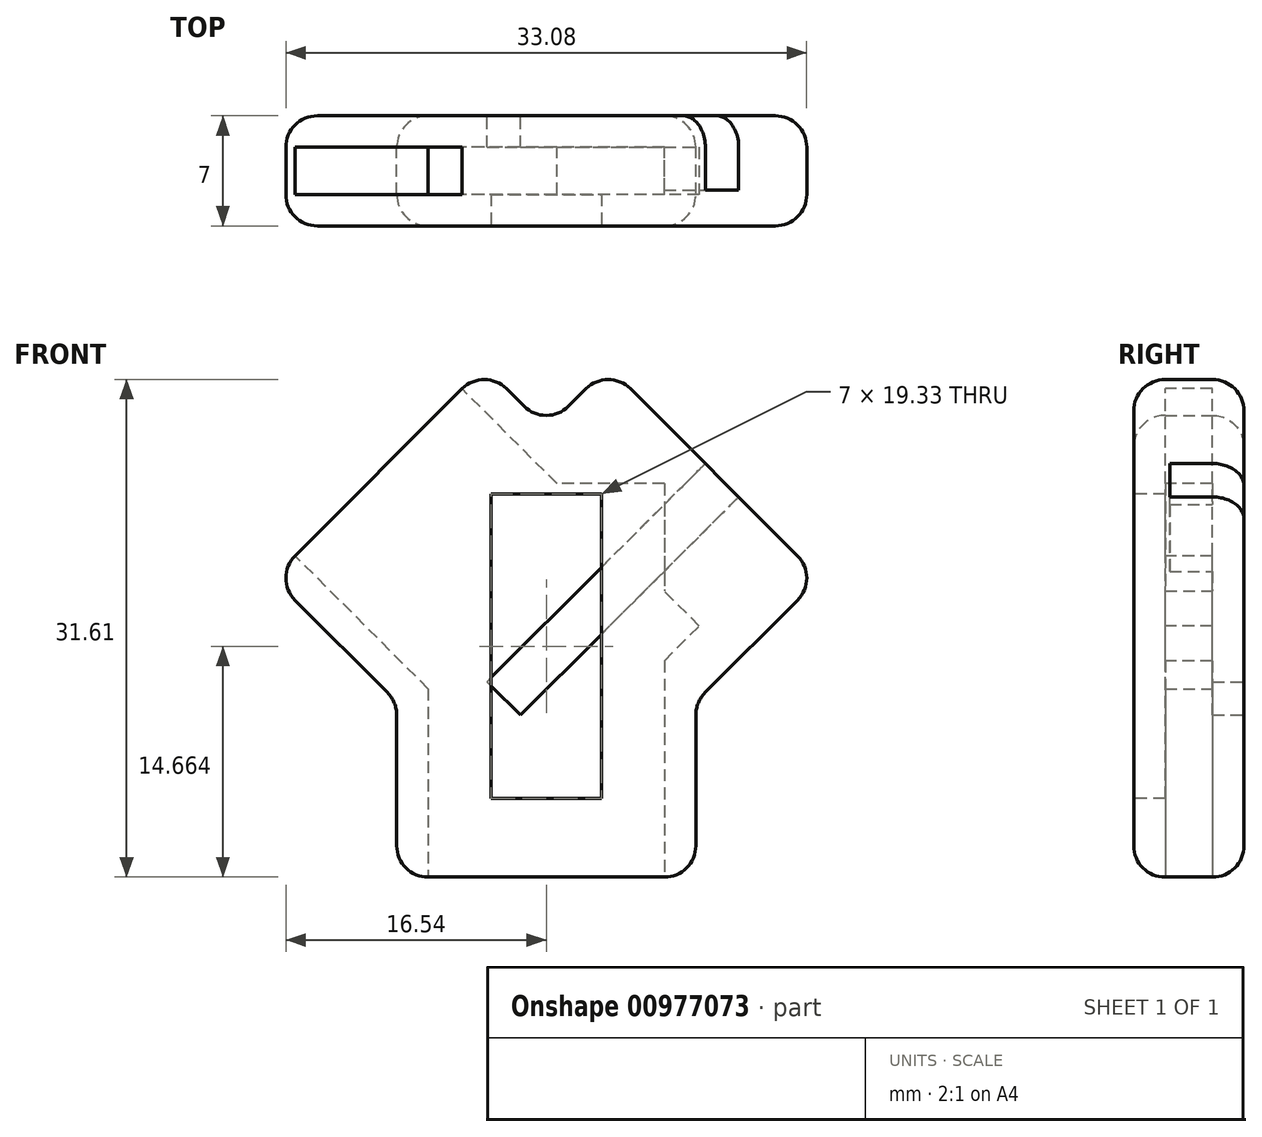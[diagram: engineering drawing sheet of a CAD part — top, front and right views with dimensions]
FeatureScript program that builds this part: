
annotation { "Feature Type Name" : "Feature", "Feature Type Description" : "" }
export const myFeature = defineFeature(function(context is Context, id is Id, definition is map)
    precondition{}
    {
        {
            var Q0;
            Q0=qCreatedBy(makeId("Front.planeOp"),FACE);
            var sketch = newSketch(context, id + "F0", { "sketchPlane" : qUnion([Q0])});
            skLineSegment(sketch, "E0.bottom", {"start": v(-9.5, 0) * mm, "end": v(9.5, 0) * mm});
            skLineSegment(sketch, "E0.top", {"start": v(-9.5, -19) * mm, "end": v(9.5, -19) * mm});
            skLineSegment(sketch, "E0.left", {"start": v(-9.5, 0) * mm, "end": v(-9.5, -19) * mm});
            skLineSegment(sketch, "E0.right", {"start": v(9.5, 0) * mm, "end": v(9.5, -19) * mm});
            skLineSegment(sketch, "E1", {"start": v(-9.5, 0) * mm, "end": v(3.94, 13.44) * mm});
            skLineSegment(sketch, "E2", {"start": v(3.94, 13.44) * mm, "end": v(17.37, 0) * mm});
            skLineSegment(sketch, "E3", {"start": v(17.37, 0) * mm, "end": v(9.5, -7.87) * mm});
            skLineSegment(sketch, "E4", {"start": v(9.5, -7.87) * mm, "end": v(9.5, 0) * mm});
            skLineSegment(sketch, "E5", {"start": v(9.5, 0) * mm, "end": v(-3.94, 13.44) * mm});
            skLineSegment(sketch, "E6", {"start": v(-3.94, 13.44) * mm, "end": v(-17.37, 0) * mm});
            skLineSegment(sketch, "E7", {"start": v(-17.37, 0) * mm, "end": v(-9.5, -7.87) * mm});
            skSolve(sketch);
        }
        {
            var Q0;
            Q0 = qSketchRegion(id + "F0", true);
            extrude(context, id + "F1", {"entities" : qUnion([Q0]), "depth" : 7 * mm, "offsetDistance" : 25 * mm});
        }
        {
            var Q0;
            Q0=makeQuery(id+"F1.opExtrude","SWEPT_FACE",FACE,{"disambiguationData":[OSD([sQuery(id+"F0.wireOp",EDGE,"E0.top")])]});
            var sketch = newSketch(context, id + "F2", { "sketchPlane" : qUnion([Q0])});
            skLineSegment(sketch, "E8.bottom", {"start": v(7.5, 2) * mm, "end": v(-7.5, 2) * mm});
            skLineSegment(sketch, "E8.top", {"start": v(7.5, 5) * mm, "end": v(-7.5, 5) * mm});
            skLineSegment(sketch, "E8.left", {"start": v(7.5, 2) * mm, "end": v(7.5, 5) * mm});
            skLineSegment(sketch, "E8.right", {"start": v(-7.5, 2) * mm, "end": v(-7.5, 5) * mm});
            skPoint(sketch, "E8.middle", {"position": v(0, 3.5) * mm});
            skPoint(sketch, "E8.middle.positionSnap0", {"position": v(0, 7) * mm});
            skPoint(sketch, "E8.middle.positionSnap1", {"position": v(-9.5, 3.5) * mm});
            skPoint(sketch, "E8.centerSnap0", {"position": v(0, 7) * mm});
            skPoint(sketch, "E8.centerSnap1", {"position": v(-9.5, 3.5) * mm});
            skSolve(sketch);
        }
        {
            var Q0;
            Q0 = qSketchRegion(id + "F2", true);
            extrude(context, id + "F3", {"entities" : qUnion([Q0]), "operationType" : NewBodyOperationType.REMOVE, "oppositeDirection" : true, "depth" : 25 * mm, "offsetDistance" : 25 * mm});
        }
        {
            var Q0;
            Q0=makeQuery(id+"F1.opExtrude","SWEPT_FACE",FACE,{"disambiguationData":[OSD([sQuery(id+"F0.wireOp",EDGE,"E2")])]});
            var sketch = newSketch(context, id + "F4", { "sketchPlane" : qUnion([Q0])});
            skLineSegment(sketch, "E9.bottom", {"start": v(-4.72, -2) * mm, "end": v(10.28, -2) * mm});
            skLineSegment(sketch, "E9.top", {"start": v(-4.72, -5) * mm, "end": v(10.28, -5) * mm});
            skLineSegment(sketch, "E9.left", {"start": v(-4.72, -2) * mm, "end": v(-4.72, -5) * mm});
            skLineSegment(sketch, "E9.right", {"start": v(10.28, -2) * mm, "end": v(10.28, -5) * mm});
            skPoint(sketch, "E9.middle", {"position": v(2.78, -3.5) * mm});
            skPoint(sketch, "E9.middle.positionSnap0", {"position": v(12.28, -3.5) * mm});
            skPoint(sketch, "E9.middle.positionSnap1", {"position": v(2.78, 0) * mm});
            skPoint(sketch, "E9.centerSnap0", {"position": v(12.28, -3.5) * mm});
            skPoint(sketch, "E9.centerSnap1", {"position": v(2.78, 0) * mm});
            skSolve(sketch);
        }
        {
            var Q0;
            Q0 = qSketchRegion(id + "F4", true);
            extrude(context, id + "F5", {"entities" : qUnion([Q0]), "operationType" : NewBodyOperationType.REMOVE, "oppositeDirection" : true, "depth" : 19.6 * mm, "offsetDistance" : 25 * mm});
        }
        {
            var Q0;
            Q0=makeQuery(id+"F1.opExtrude","SWEPT_FACE",FACE,{"disambiguationData":[OSD([sQuery(id+"F0.wireOp",EDGE,"E6")])]});
            var sketch = newSketch(context, id + "F6", { "sketchPlane" : qUnion([Q0])});
            skLineSegment(sketch, "E10.bottom", {"start": v(2, -10.28) * mm, "end": v(5, -10.28) * mm});
            skLineSegment(sketch, "E10.top", {"start": v(2, 4.72) * mm, "end": v(5, 4.72) * mm});
            skLineSegment(sketch, "E10.left", {"start": v(2, -10.28) * mm, "end": v(2, 4.72) * mm});
            skLineSegment(sketch, "E10.right", {"start": v(5, -10.28) * mm, "end": v(5, 4.72) * mm});
            skPoint(sketch, "E10.middle", {"position": v(3.5, -2.78) * mm});
            skPoint(sketch, "E10.middle.positionSnap0", {"position": v(0, -2.78) * mm});
            skPoint(sketch, "E10.middle.positionSnap1", {"position": v(3.5, 6.72) * mm});
            skPoint(sketch, "E10.centerSnap0", {"position": v(0, -2.78) * mm});
            skPoint(sketch, "E10.centerSnap1", {"position": v(3.5, 6.72) * mm});
            skSolve(sketch);
        }
        {
            var Q0;
            Q0 = qSketchRegion(id + "F6", true);
            extrude(context, id + "F7", {"entities" : qUnion([Q0]), "operationType" : NewBodyOperationType.REMOVE, "oppositeDirection" : true, "depth" : 21.3 * mm, "offsetDistance" : 25 * mm});
        }
        {
            var Q0;
            Q0=makeQuery(id+"F1.opExtrude","CAP_EDGE",EDGE,{"disambiguationData":[OSD([sQuery(id+"F0.wireOp",EDGE,"E0.left")])],"isStart":false});
            var Q1;
            Q1=makeQuery(id+"F1.opExtrude","CAP_EDGE",EDGE,{"disambiguationData":[OSD([sQuery(id+"F0.wireOp",EDGE,"E7")])],"isStart":false});
            var Q2;
            Q2=makeQuery(id+"F1.opExtrude","CAP_EDGE",EDGE,{"disambiguationData":[OSD([sQuery(id+"F0.wireOp",EDGE,"E7")])],"isStart":true});
            var Q3;
            Q3=makeQuery(id+"F1.opExtrude","CAP_EDGE",EDGE,{"disambiguationData":[OSD([sQuery(id+"F0.wireOp",EDGE,"E0.left")])],"isStart":true});
            var Q4;
            Q4=makeQuery(id+"F1.opExtrude","CAP_EDGE",EDGE,{"disambiguationData":[OSD([sQuery(id+"F0.wireOp",EDGE,"E0.top")])],"isStart":false});
            var Q5;
            Q5=makeQuery(id+"F1.opExtrude","CAP_EDGE",EDGE,{"disambiguationData":[OSD([sQuery(id+"F0.wireOp",EDGE,"E0.top")])],"isStart":true});
            var Q6;
            Q6=makeQuery(id+"F1.opExtrude","SWEPT_EDGE",EDGE,{"disambiguationData":[OSD([sQuery(id+"F0.wireOp",EDGE,"E0.top"),sQuery(id+"F0.wireOp",EDGE,"E0.left")])]});
            var Q7;
            Q7=makeQuery(id+"F1.opExtrude","SWEPT_EDGE",EDGE,{"disambiguationData":[OSD([sQuery(id+"F0.wireOp",EDGE,"E0.top"),sQuery(id+"F0.wireOp",EDGE,"E0.right")])]});
            var Q8;
            Q8=makeQuery(id+"F1.opExtrude","CAP_EDGE",EDGE,{"disambiguationData":[OSD([sQuery(id+"F0.wireOp",EDGE,"E0.right")])],"isStart":false});
            var Q9;
            Q9=makeQuery(id+"F1.opExtrude","CAP_EDGE",EDGE,{"disambiguationData":[OSD([sQuery(id+"F0.wireOp",EDGE,"E0.right")])],"isStart":true});
            var Q10;
            Q10=makeQuery(id+"F1.opExtrude","CAP_EDGE",EDGE,{"disambiguationData":[OSD([sQuery(id+"F0.wireOp",EDGE,"E3")])],"isStart":true});
            var Q11;
            Q11=makeQuery(id+"F1.opExtrude","CAP_EDGE",EDGE,{"disambiguationData":[OSD([sQuery(id+"F0.wireOp",EDGE,"E3")])],"isStart":false});
            var Q12;
            Q12=makeQuery(id+"F1.opExtrude","SWEPT_EDGE",EDGE,{"disambiguationData":[OSD([sQuery(id+"F0.wireOp",EDGE,"E2"),sQuery(id+"F0.wireOp",EDGE,"E3")])]});
            var Q13;
            Q13=makeQuery(id+"F1.opExtrude","CAP_EDGE",EDGE,{"disambiguationData":[OSD([sQuery(id+"F0.wireOp",EDGE,"E2")])],"isStart":false});
            var Q14;
            Q14=makeQuery(id+"F1.opExtrude","SWEPT_EDGE",EDGE,{"disambiguationData":[OSD([sQuery(id+"F0.wireOp",EDGE,"E1"),sQuery(id+"F0.wireOp",EDGE,"E2")])]});
            var Q15;
            Q15=makeQuery(id+"F1.opExtrude","CAP_EDGE",EDGE,{"disambiguationData":[OSD([sQuery(id+"F0.wireOp",EDGE,"E2")])],"isStart":true});
            var Q16;
            Q16=makeQuery(id+"F1.opExtrude","CAP_EDGE",EDGE,{"disambiguationData":[OSD([sQuery(id+"F0.wireOp",EDGE,"E1")])],"isStart":true});
            var Q17;
            Q17=makeQuery(id+"F1.opExtrude","CAP_EDGE",EDGE,{"disambiguationData":[OSD([sQuery(id+"F0.wireOp",EDGE,"E5")])],"isStart":true});
            var Q18;
            Q18=makeQuery(id+"F1.opExtrude","CAP_EDGE",EDGE,{"disambiguationData":[OSD([sQuery(id+"F0.wireOp",EDGE,"E5")])],"isStart":false});
            var Q19;
            Q19=makeQuery(id+"F1.opExtrude","CAP_EDGE",EDGE,{"disambiguationData":[OSD([sQuery(id+"F0.wireOp",EDGE,"E1")])],"isStart":false});
            var Q20;
            Q20=makeQuery(id+"F1.opExtrude","CAP_EDGE",EDGE,{"disambiguationData":[OSD([sQuery(id+"F0.wireOp",EDGE,"E6")])],"isStart":false});
            var Q21;
            Q21=makeQuery(id+"F1.opExtrude","SWEPT_EDGE",EDGE,{"disambiguationData":[OSD([sQuery(id+"F0.wireOp",EDGE,"E5"),sQuery(id+"F0.wireOp",EDGE,"E6")])]});
            var Q22;
            Q22=makeQuery(id+"F1.opExtrude","CAP_EDGE",EDGE,{"disambiguationData":[OSD([sQuery(id+"F0.wireOp",EDGE,"E6")])],"isStart":true});
            var Q23;
            Q23=makeQuery(id+"F1.opExtrude","SWEPT_EDGE",EDGE,{"disambiguationData":[OSD([sQuery(id+"F0.wireOp",EDGE,"E6"),sQuery(id+"F0.wireOp",EDGE,"E7")])]});
            var Q24;
            Q24=makeQuery(id+"F1.opExtrude","SWEPT_EDGE",EDGE,{"disambiguationData":[OSD([sQuery(id+"F0.wireOp",EDGE,"E1"),sQuery(id+"F0.wireOp",EDGE,"E5")])]});
            var Q25;
            Q25=makeQuery(id+"F1.opExtrude","SWEPT_EDGE",EDGE,{"disambiguationData":[OSD([sQuery(id+"F0.wireOp",EDGE,"E0.left"),sQuery(id+"F0.wireOp",EDGE,"E7")])]});
            var Q26;
            Q26=makeQuery(id+"F1.opExtrude","SWEPT_EDGE",EDGE,{"disambiguationData":[OSD([sQuery(id+"F0.wireOp",EDGE,"E0.right"),sQuery(id+"F0.wireOp",EDGE,"E3"),sQuery(id+"F0.wireOp",EDGE,"E4")])]});
            fillet(context, id + "F8", {"entities" : qUnion([Q0, Q1, Q2, Q3, Q4, Q5, Q6, Q7, Q8, Q9, Q10, Q11, Q12, Q13, Q14, Q15, Q16, Q17, Q18, Q19, Q20, Q21, Q22, Q23, Q24, Q25, Q26]), "radius" : 2 * mm, "tangentPropagation" : true, "allowEdgeOverflow" : false});
        }
        {
            var Q0;
            Q0=makeQuery(id+"F1.opExtrude","CAP_FACE",FACE,{"disambiguationData":[OSD([sQuery(id+"F0.wireOp",EDGE,"E0.top"),sQuery(id+"F0.wireOp",EDGE,"E0.left"),sQuery(id+"F0.wireOp",EDGE,"E0.right"),sQuery(id+"F0.wireOp",EDGE,"E1"),sQuery(id+"F0.wireOp",EDGE,"E2"),sQuery(id+"F0.wireOp",EDGE,"E3"),sQuery(id+"F0.wireOp",EDGE,"E5"),sQuery(id+"F0.wireOp",EDGE,"E6"),sQuery(id+"F0.wireOp",EDGE,"E7")])],"isStart":false});
            var sketch = newSketch(context, id + "F9", { "sketchPlane" : qUnion([Q0])});
            skLineSegment(sketch, "E11.bottom", {"start": v(-3.5, -14) * mm, "end": v(3.5, -14) * mm});
            skLineSegment(sketch, "E11.top", {"start": v(-3.5, 5.33) * mm, "end": v(3.5, 5.33) * mm});
            skLineSegment(sketch, "E11.left", {"start": v(-3.5, -14) * mm, "end": v(-3.5, 5.33) * mm});
            skLineSegment(sketch, "E11.right", {"start": v(3.5, -14) * mm, "end": v(3.5, 5.33) * mm});
            skSolve(sketch);
        }
        {
            var Q0;
            Q0 = qSketchRegion(id + "F9", true);
            extrude(context, id + "F10", {"entities" : qUnion([Q0]), "operationType" : NewBodyOperationType.REMOVE, "oppositeDirection" : true, "depth" : 2 * mm, "offsetDistance" : 25 * mm});
        }
    });
